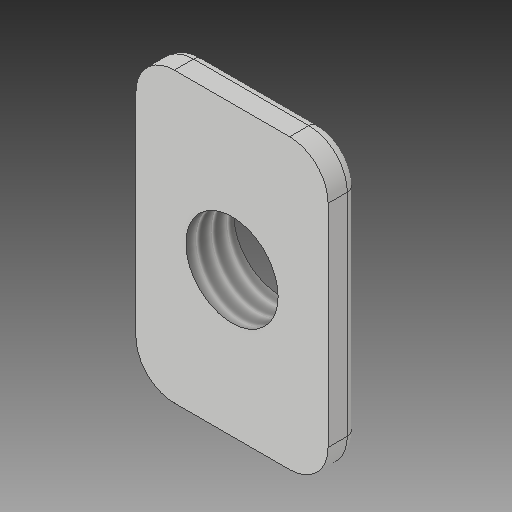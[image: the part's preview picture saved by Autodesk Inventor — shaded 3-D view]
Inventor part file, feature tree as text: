
AUTODESK INVENTOR PART (.ipt)
format: ipt  version: 2017 (Build 210142000, 142)  size: 145,920 bytes
history: native  units: mm
features: other x3, sketch x2
ambient origin geometry x8: Origin, YZ Plane, XZ Plane, XY Plane, X Axis, Y Axis, Z Axis, Center Point
bodies: Solid1 (feature_tree)
feature tree (5):
  other  "M5 Tee Nut_MIR_MIR_MIR_MIR.ipt"
  other  "Solid1::M5 Tee Nut_MIR_MIR_MIR_MIR.ipt"
  other  "TaggingFeature1"
  sketch  "Sketch1"  dims[d0=10.0mm]
  sketch  "Sketch2"
